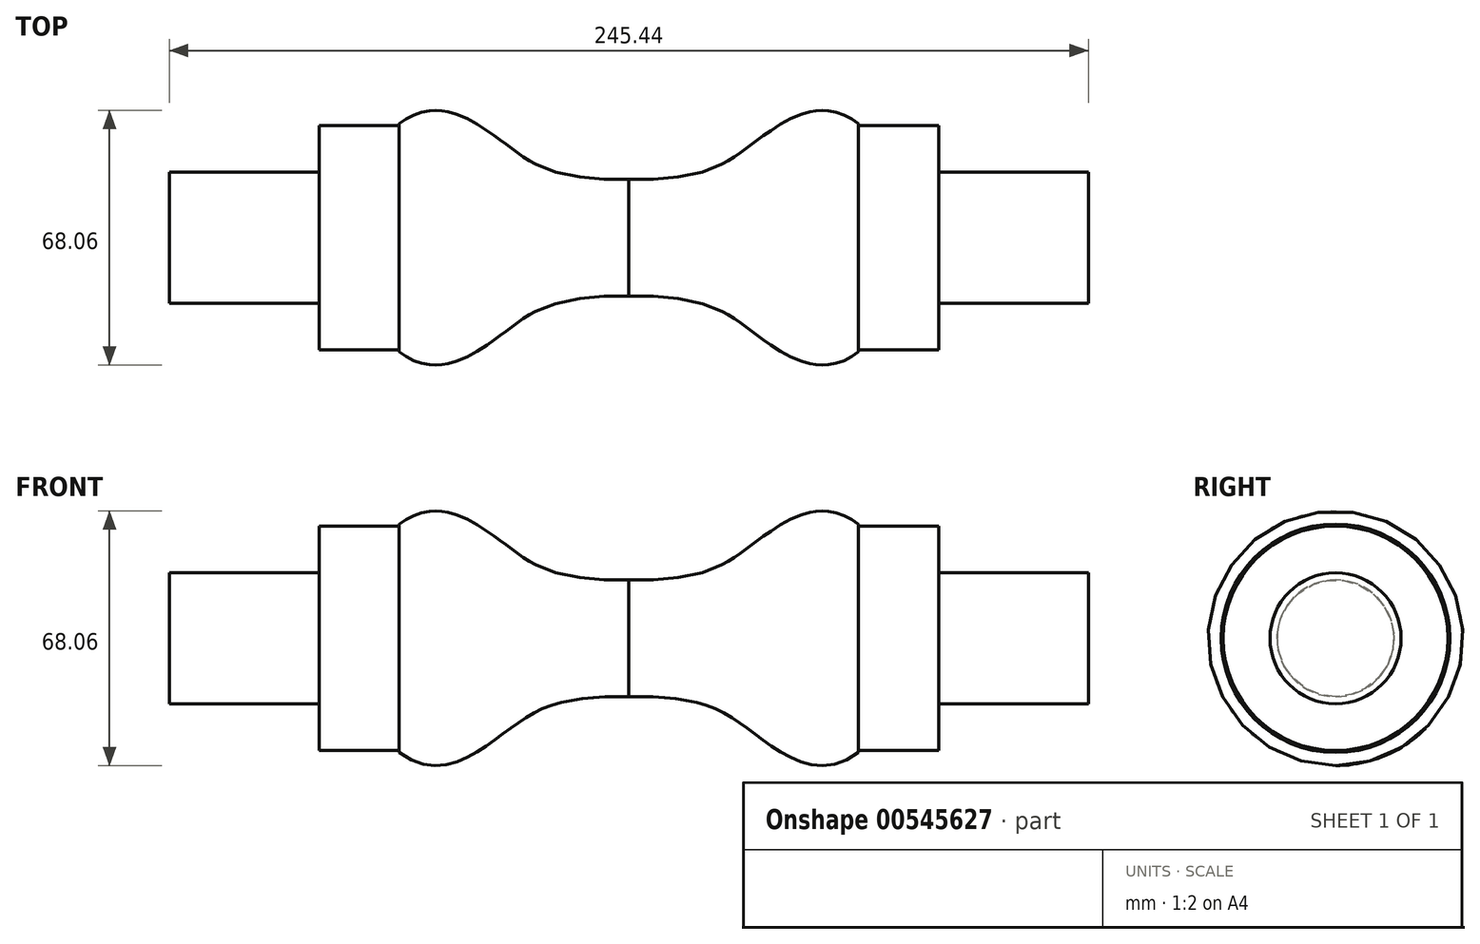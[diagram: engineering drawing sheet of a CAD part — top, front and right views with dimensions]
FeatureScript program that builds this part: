
annotation { "Feature Type Name" : "Feature", "Feature Type Description" : "" }
export const myFeature = defineFeature(function(context is Context, id is Id, definition is map)
    precondition{}
    {
        {
            var Q0;
            Q0=qCreatedBy(makeId("Front.planeOp"),FACE);
            var sketch = newSketch(context, id + "F0", { "sketchPlane" : qUnion([Q0])});
            skLineSegment(sketch, "E0", {"start": v(0, 0) * mm, "end": v(0, 15.62) * mm});
            skLineSegment(sketch, "E1", {"start": v(61.36, 30) * mm, "end": v(61.36, 30.54) * mm});
            skLineSegment(sketch, "E2", {"start": v(61.36, 30) * mm, "end": v(82.72, 30) * mm});
            skLineSegment(sketch, "E3", {"start": v(82.72, 30) * mm, "end": v(82.72, 17.5) * mm});
            skLineSegment(sketch, "E4", {"start": v(82.72, 17.5) * mm, "end": v(122.72, 17.5) * mm});
            skLineSegment(sketch, "E5", {"start": v(122.72, 17.5) * mm, "end": v(122.72, 0) * mm});
            skLineSegment(sketch, "E6", {"start": v(122.72, 0) * mm, "end": v(0, 0) * mm});
            skFitSpline(sketch, "E7", {"points": [v(0, 15.62) * mm, v(23.05, 18.8) * mm, v(38.1, 28.78) * mm, v(61.36, 30.54) * mm], "startDerivative": vector(75.16, -1.55) * mm, "endDerivative": vector(75.73, -57.45) * mm});
            skSolve(sketch);
        }
        {
            var Q0;
            Q0=makeQuery(id+"F0.imprint","IMPRINT",FACE,{"disambiguationData":[TD([[makeQuery(id+"F0.imprint","IMPRINT",EDGE,{"derivedFrom":sQuery(id+"F0.wireOp",EDGE,"E0")}),-1.0]])]});
            var Q1;
            Q1=sQuery(id+"F0.wireOp",EDGE,"E6");
            revolve(context, id + "F1", {"entities" : qUnion([Q0]), "axis" : qUnion([Q1]), "revolveType" : RevolveType.FULL});
        }
        {
            var Q0;
            Q0=makeQuery(id+"F1.opRevolve","SWEPT_BODY",BODY,{"disambiguationData":[OSD([sQuery(id+"F0.wireOp",EDGE,"E0"),sQuery(id+"F0.wireOp",EDGE,"E1"),sQuery(id+"F0.wireOp",EDGE,"E2"),sQuery(id+"F0.wireOp",EDGE,"E3"),sQuery(id+"F0.wireOp",EDGE,"E4"),sQuery(id+"F0.wireOp",EDGE,"E5"),sQuery(id+"F0.wireOp",EDGE,"E6"),sQuery(id+"F0.wireOp",EDGE,"E7")])]});
            var Q1;
            Q1=makeQuery(id+"F1.opRevolve","SWEPT_FACE",FACE,{"disambiguationData":[OSD([sQuery(id+"F0.wireOp",EDGE,"E0")])]});
            mirror(context, id + "F2", {"operationType" : NewBodyOperationType.ADD, "entities" : qUnion([Q0]), "mirrorPlane" : qUnion([Q1])});
        }
    });
